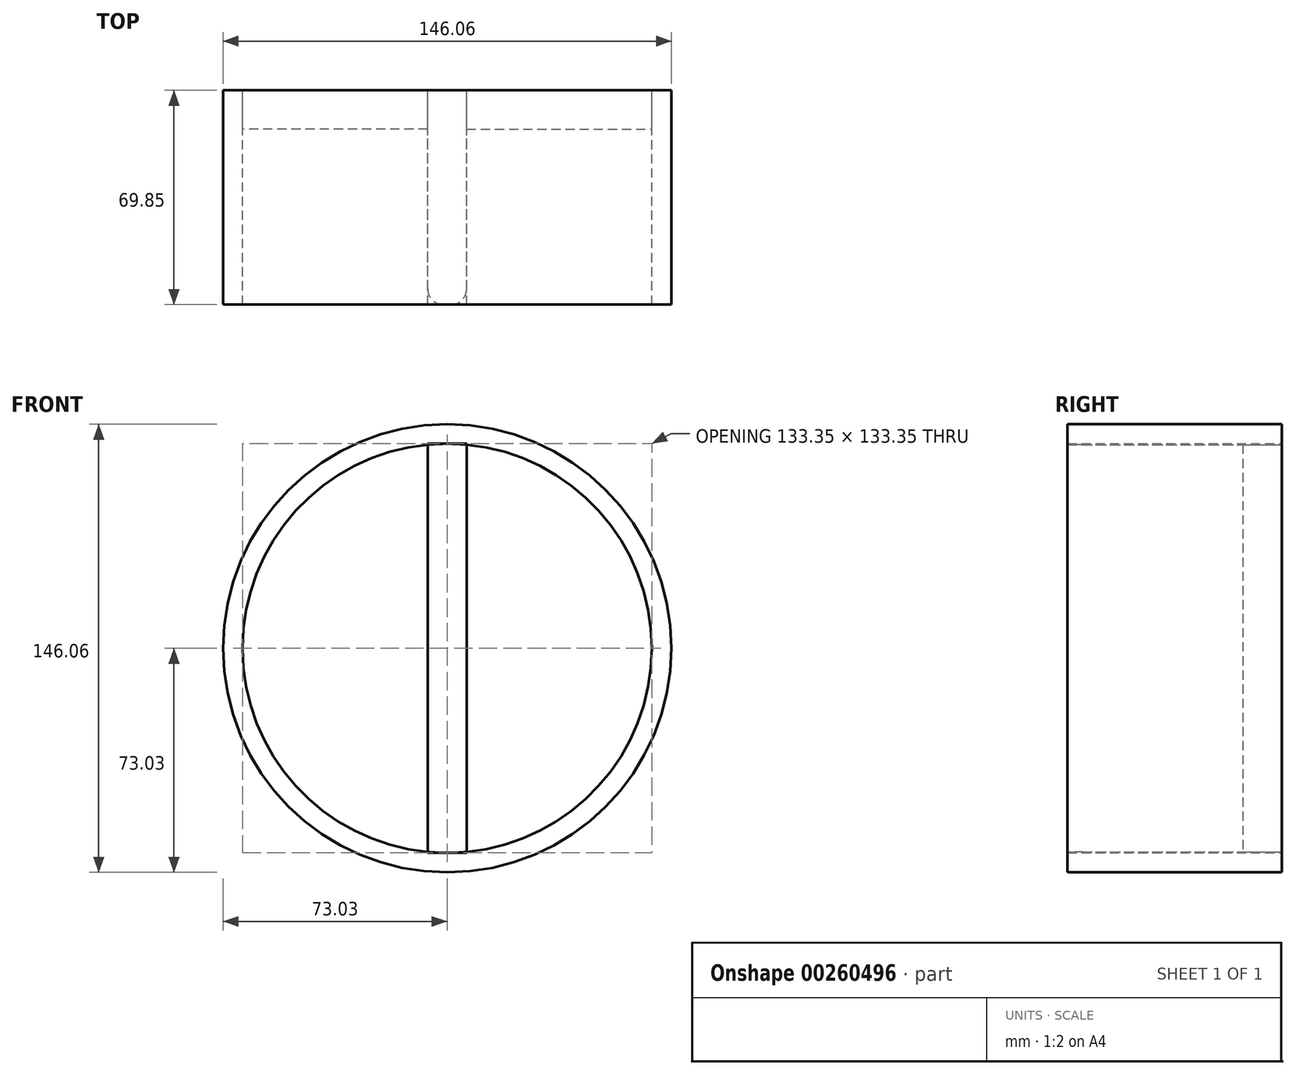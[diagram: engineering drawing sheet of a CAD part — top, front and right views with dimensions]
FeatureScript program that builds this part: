
annotation { "Feature Type Name" : "Feature", "Feature Type Description" : "" }
export const myFeature = defineFeature(function(context is Context, id is Id, definition is map)
    precondition{}
    {
        {
            var Q0;
            Q0=qCreatedBy(makeId("Front.planeOp"),FACE);
            var sketch = newSketch(context, id + "F0", { "sketchPlane" : qUnion([Q0])});
            skCircle(sketch, "E0", {"center": v(0, 0) * mm, "radius": 73.03 * mm});
            skCircle(sketch, "E1", {"center": v(0, 0) * mm, "radius": 66.68 * mm});
            skLineSegment(sketch, "E2.bottom", {"start": v(0, 66.68) * mm, "end": v(0, 66.68) * mm});
            skLineSegment(sketch, "E2.top", {"start": v(0, -66.68) * mm, "end": v(0, -66.68) * mm});
            skLineSegment(sketch, "E3.bottom", {"start": v(6.35, 66.68) * mm, "end": v(-6.35, 66.68) * mm});
            skLineSegment(sketch, "E3.top", {"start": v(6.35, -66.68) * mm, "end": v(-6.35, -66.68) * mm});
            skLineSegment(sketch, "E3.left", {"start": v(6.35, 66.68) * mm, "end": v(6.35, -66.68) * mm});
            skLineSegment(sketch, "E3.right", {"start": v(-6.35, 66.68) * mm, "end": v(-6.35, -66.68) * mm});
            skSolve(sketch);
        }
        {
            var Q0;
            Q0=makeQuery(id+"F0.imprint","IMPRINT",FACE,{"disambiguationData":[TD([[makeQuery(id+"F0.imprint","IMPRINT",EDGE,{"derivedFrom":sQuery(id+"F0.wireOp",EDGE,"E0")}),1.0]])]});
            var Q1;
            {var subQ0=sQuery(id+"F0.wireOp",EDGE,"E1");var subQ7=makeQuery(id+"F0.imprint","INTERSECT",VERTEX,{"derivedFrom":[subQ0,sQuery(id+"F0.wireOp",EDGE,"E3.bottom")]});Q1=makeQuery(id+"F0.imprint","IMPRINT",FACE,{"disambiguationData":[TD([[makeQuery(id+"F0.imprint","IMPRINT",EDGE,{"disambiguationData":[TD([[subQ7,1.0]])],"derivedFrom":subQ0}),1.0]])]});}
            extrude(context, id + "F1", {"entities" : qUnion([Q0, Q1]), "depth" : 69.85 * mm});
        }
        {
            var Q0;
            {var subQ0=sQuery(id+"F0.wireOp",EDGE,"E3.right");var subQ1=sQuery(id+"F0.wireOp",EDGE,"E1");var subQ2=makeQuery(id+"F0.imprint","INTERSECT",VERTEX,{"disambiguationData":[OD(0.0)],"derivedFrom":[subQ1,subQ0]});Q0=makeQuery(id+"F0.imprint","IMPRINT",FACE,{"disambiguationData":[TD([[makeQuery(id+"F0.imprint","IMPRINT",EDGE,{"disambiguationData":[TD([[subQ2,-1.0]])],"derivedFrom":subQ1}),1.0]])]});}
            var Q1;
            {var subQ0=sQuery(id+"F0.wireOp",EDGE,"E3.left");var subQ1=sQuery(id+"F0.wireOp",EDGE,"E1");var subQ2=makeQuery(id+"F0.imprint","INTERSECT",VERTEX,{"disambiguationData":[OD(0.0)],"derivedFrom":[subQ1,subQ0]});Q1=makeQuery(id+"F0.imprint","IMPRINT",FACE,{"disambiguationData":[TD([[makeQuery(id+"F0.imprint","IMPRINT",EDGE,{"disambiguationData":[TD([[subQ2,1.0]])],"derivedFrom":subQ1}),1.0]])]});}
            extrude(context, id + "F2", {"entities" : qUnion([Q0, Q1]), "depth" : 12.7 * mm});
        }
        {
            var Q0;
            {var subQ0=sQuery(id+"F0.wireOp",EDGE,"E3.left");var subQ1=sQuery(id+"F0.wireOp",EDGE,"E1");Q0=makeQuery(id+"F1.opExtrude","CAP_EDGE",EDGE,{"disambiguationData":[OSD([subQ0]),TDD([makeQuery(id+"F0.imprint","IMPRINT",EDGE,{"disambiguationData":[TD([[makeQuery(id+"F0.imprint","INTERSECT",VERTEX,{"disambiguationData":[OD(0.0)],"derivedFrom":[subQ1,subQ0]}),-1.0]])],"derivedFrom":subQ0})])],"isStart":false});}
            var Q1;
            {var subQ0=sQuery(id+"F0.wireOp",EDGE,"E3.right");var subQ1=sQuery(id+"F0.wireOp",EDGE,"E1");Q1=makeQuery(id+"F1.opExtrude","CAP_EDGE",EDGE,{"disambiguationData":[OSD([subQ0]),TDD([makeQuery(id+"F0.imprint","IMPRINT",EDGE,{"disambiguationData":[TD([[makeQuery(id+"F0.imprint","INTERSECT",VERTEX,{"disambiguationData":[OD(0.0)],"derivedFrom":[subQ1,subQ0]}),-1.0]])],"derivedFrom":subQ0})])],"isStart":false});}
            fillet(context, id + "F3", {"entities" : qUnion([Q0, Q1]), "radius" : 5.08 * mm, "tangentPropagation" : true, "allowEdgeOverflow" : false});
        }
    });
